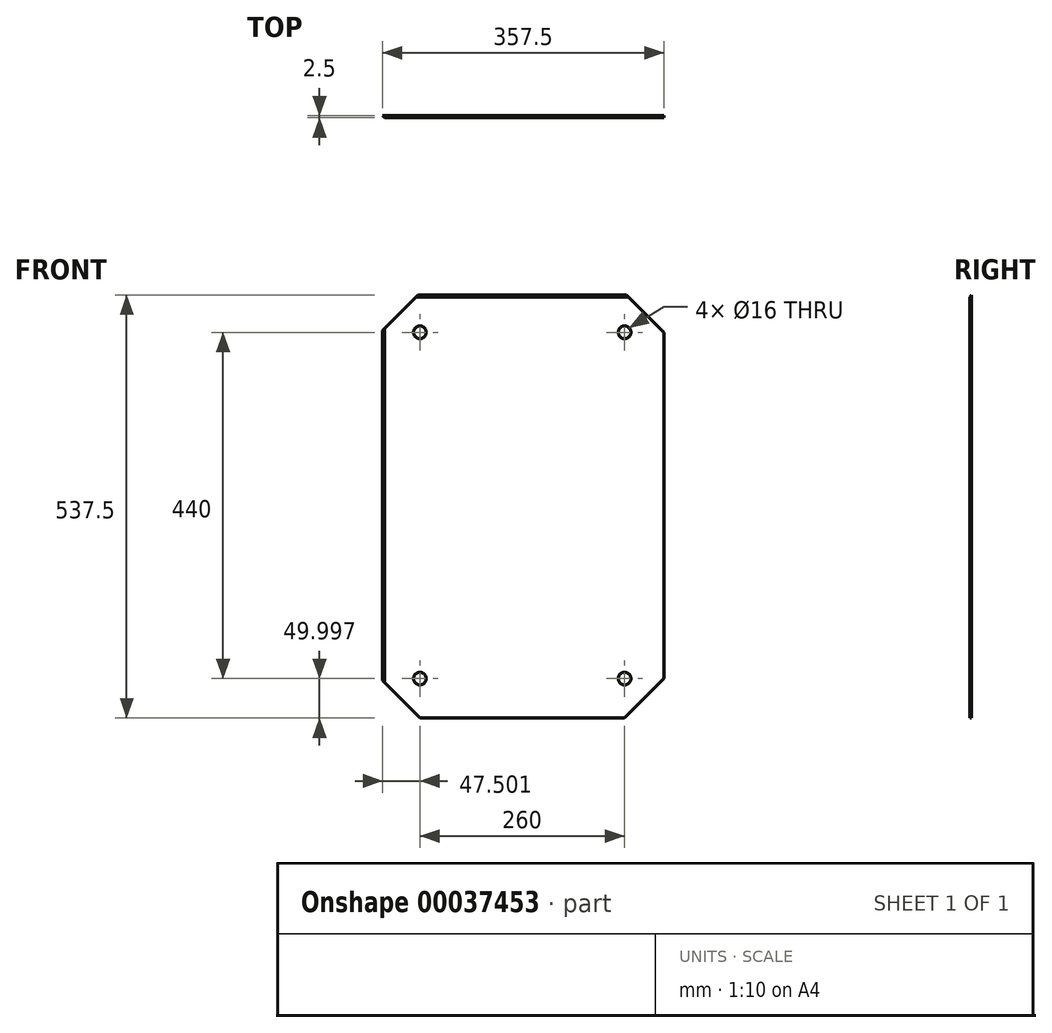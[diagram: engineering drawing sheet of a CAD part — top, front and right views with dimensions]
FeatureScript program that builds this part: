
annotation { "Feature Type Name" : "Feature", "Feature Type Description" : "" }
export const myFeature = defineFeature(function(context is Context, id is Id, definition is map)
    precondition{}
    {
        {
            var Q0;
            Q0=qCreatedBy(makeId("Front.planeOp"),FACE);
            var sketch = newSketch(context, id + "F0", { "sketchPlane" : qUnion([Q0])});
            skLineSegment(sketch, "E0.bottom", {"start": v(13.16, 523.12) * mm, "end": v(273.16, 523.12) * mm});
            skLineSegment(sketch, "E0.top", {"start": v(13.16, -16.88) * mm, "end": v(273.16, -16.88) * mm});
            skLineSegment(sketch, "E0.left", {"start": v(-36.84, 473.12) * mm, "end": v(-36.84, 33.12) * mm});
            skLineSegment(sketch, "E0.right", {"start": v(323.16, 473.12) * mm, "end": v(323.16, 33.12) * mm});
            skLineSegment(sketch, "E1", {"start": v(-65.72, 473.12) * mm, "end": v(526.37, 473.12) * mm, "construction": true});
            skLineSegment(sketch, "E2", {"start": v(273.16, 624.8) * mm, "end": v(273.16, -56.18) * mm, "construction": true});
            skLineSegment(sketch, "E3", {"start": v(13.16, 571.31) * mm, "end": v(13.16, -75.62) * mm, "construction": true});
            skLineSegment(sketch, "E4", {"start": v(-160.05, 33.12) * mm, "end": v(470.26, 33.12) * mm, "construction": true});
            skCircle(sketch, "E5", {"center": v(13.16, 473.12) * mm, "radius": 8 * mm});
            skCircle(sketch, "E6", {"center": v(273.16, 473.12) * mm, "radius": 8 * mm});
            skCircle(sketch, "E7", {"center": v(13.16, 33.12) * mm, "radius": 8 * mm});
            skCircle(sketch, "E8", {"center": v(273.16, 33.12) * mm, "radius": 8 * mm});
            skLineSegment(sketch, "E9", {"start": v(13.16, 523.12) * mm, "end": v(-36.84, 473.12) * mm});
            skLineSegment(sketch, "E10", {"start": v(273.16, 523.12) * mm, "end": v(323.16, 473.12) * mm});
            skLineSegment(sketch, "E11", {"start": v(323.16, 33.12) * mm, "end": v(273.16, -16.88) * mm});
            skLineSegment(sketch, "E12", {"start": v(13.16, -16.88) * mm, "end": v(-36.84, 33.12) * mm});
            skSolve(sketch);
        }
        {
            var Q0;
            Q0=makeQuery(id+"F0.imprint","IMPRINT",FACE,{"disambiguationData":[TD([[makeQuery(id+"F0.imprint","IMPRINT",EDGE,{"derivedFrom":sQuery(id+"F0.wireOp",EDGE,"E0.bottom")}),-1.0]])]});
            extrude(context, id + "F1", {"entities" : qUnion([Q0]), "depth" : 2.5 * mm});
        }
        {
            var Q0;
            Q0=makeQuery(id+"F1.opExtrude","CAP_EDGE",EDGE,{"disambiguationData":[OSD([sQuery(id+"F0.wireOp",EDGE,"E0.bottom")])],"isStart":false});
            var Q1;
            Q1=makeQuery(id+"F1.opExtrude","CAP_EDGE",EDGE,{"disambiguationData":[OSD([sQuery(id+"F0.wireOp",EDGE,"E0.left")])],"isStart":false});
            chamfer(context, id + "F2", {"entities" : qUnion([Q0, Q1]), "width" : 5 * mm, "tangentPropagation" : true});
        }
    });
